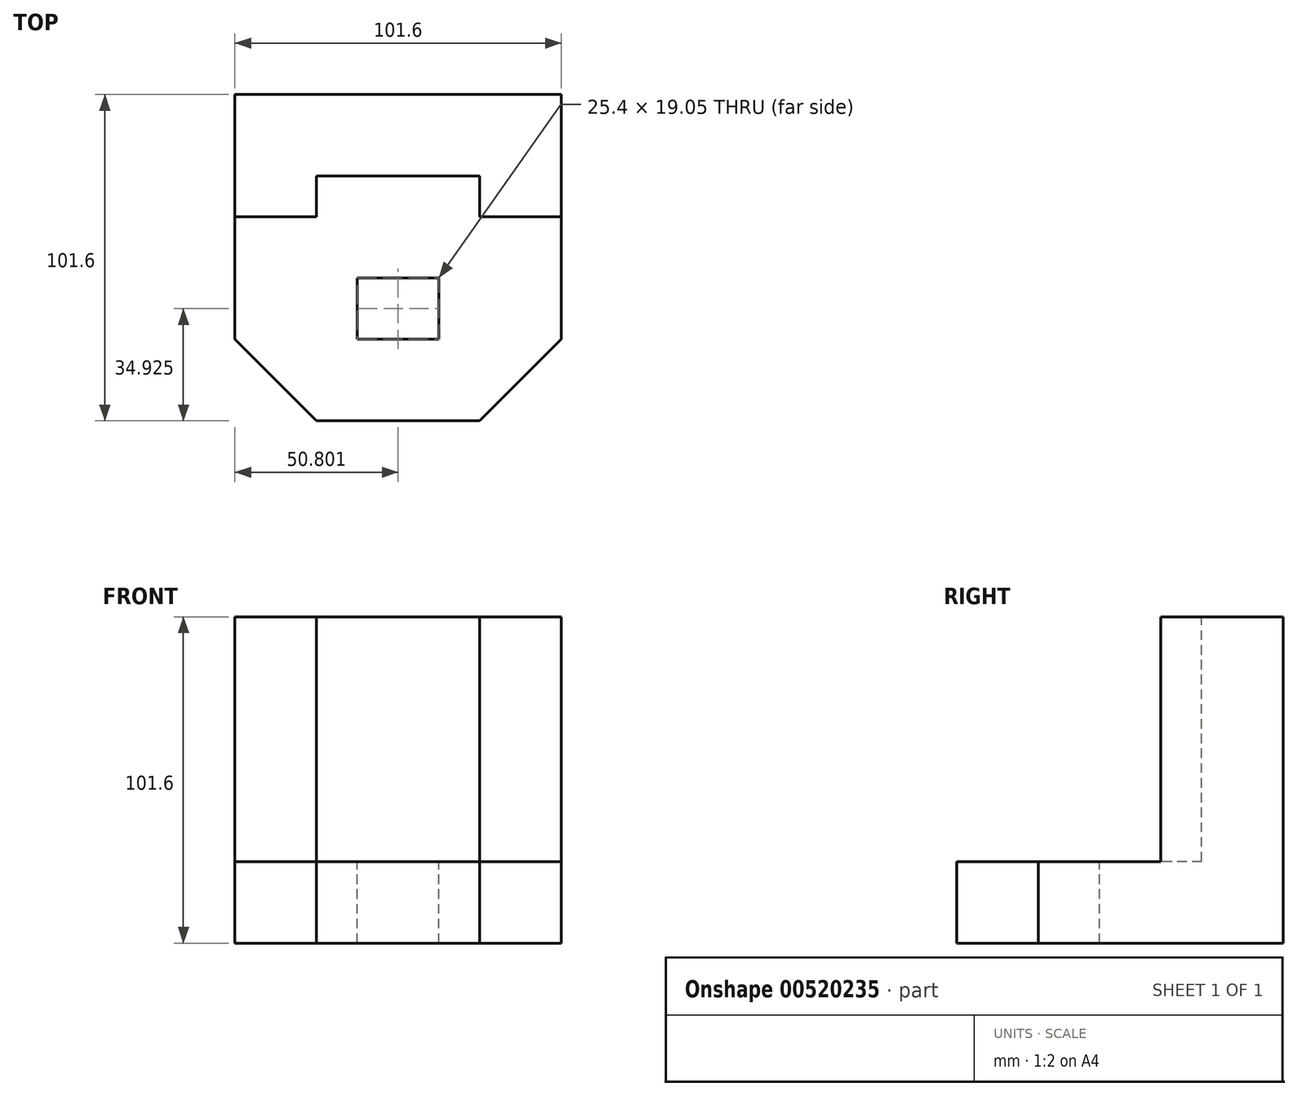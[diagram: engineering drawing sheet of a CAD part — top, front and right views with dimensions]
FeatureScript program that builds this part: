
annotation { "Feature Type Name" : "Feature", "Feature Type Description" : "" }
export const myFeature = defineFeature(function(context is Context, id is Id, definition is map)
    precondition{}
    {
        {
            var Q0;
            Q0=qCreatedBy(makeId("Front.planeOp"),FACE);
            var sketch = newSketch(context, id + "F0", { "sketchPlane" : qUnion([Q0])});
            skLineSegment(sketch, "E0.bottom", {"start": v(-47, -44.76) * mm, "end": v(54.6, -44.76) * mm});
            skLineSegment(sketch, "E0.top", {"start": v(-47, 56.84) * mm, "end": v(54.6, 56.84) * mm});
            skLineSegment(sketch, "E0.left", {"start": v(-47, -44.76) * mm, "end": v(-47, 56.84) * mm});
            skLineSegment(sketch, "E0.right", {"start": v(54.6, -44.76) * mm, "end": v(54.6, 56.84) * mm});
            skSolve(sketch);
        }
        {
            var Q0;
            Q0=makeQuery(id+"F0.imprint","IMPRINT",FACE,{"disambiguationData":[TD([[makeQuery(id+"F0.imprint","IMPRINT",EDGE,{"derivedFrom":sQuery(id+"F0.wireOp",EDGE,"E0.bottom")}),1.0]])]});
            extrude(context, id + "F1", {"entities" : qUnion([Q0]), "depth" : 101.6 * mm, "offsetDistance" : 25.4 * mm});
        }
        {
            var Q0;
            Q0=makeQuery(id+"F1.opExtrude","CAP_FACE",FACE,{"disambiguationData":[OSD([sQuery(id+"F0.wireOp",EDGE,"E0.bottom"),sQuery(id+"F0.wireOp",EDGE,"E0.top"),sQuery(id+"F0.wireOp",EDGE,"E0.left"),sQuery(id+"F0.wireOp",EDGE,"E0.right")])],"isStart":false});
            var sketch = newSketch(context, id + "F2", { "sketchPlane" : qUnion([Q0])});
            skLineSegment(sketch, "E1.bottom", {"start": v(-47, -19.36) * mm, "end": v(-21.6, -19.36) * mm});
            skLineSegment(sketch, "E1.top", {"start": v(-47, 56.84) * mm, "end": v(-21.6, 56.84) * mm});
            skLineSegment(sketch, "E1.left", {"start": v(-47, -19.36) * mm, "end": v(-47, 56.84) * mm});
            skLineSegment(sketch, "E1.right", {"start": v(-21.6, -19.36) * mm, "end": v(-21.6, 56.84) * mm});
            skLineSegment(sketch, "E2.bottom", {"start": v(54.6, -19.36) * mm, "end": v(29.2, -19.36) * mm});
            skLineSegment(sketch, "E2.top", {"start": v(54.6, 56.84) * mm, "end": v(29.2, 56.84) * mm});
            skLineSegment(sketch, "E2.left", {"start": v(54.6, -19.36) * mm, "end": v(54.6, 56.84) * mm});
            skLineSegment(sketch, "E2.right", {"start": v(29.2, -19.36) * mm, "end": v(29.2, 56.84) * mm});
            skLineSegment(sketch, "E3.bottom", {"start": v(-21.6, 56.84) * mm, "end": v(29.2, 56.84) * mm});
            skLineSegment(sketch, "E3.top", {"start": v(-21.6, -19.36) * mm, "end": v(29.2, -19.36) * mm});
            skLineSegment(sketch, "E3.left", {"start": v(-21.6, 56.84) * mm, "end": v(-21.6, -19.36) * mm});
            skLineSegment(sketch, "E3.right", {"start": v(29.2, 56.84) * mm, "end": v(29.2, -19.36) * mm});
            skSolve(sketch);
        }
        {
            var Q0;
            Q0=makeQuery(id+"F2.imprint","IMPRINT",FACE,{"disambiguationData":[TD([[makeQuery(id+"F2.imprint","IMPRINT",EDGE,{"derivedFrom":sQuery(id+"F2.wireOp",EDGE,"E3.bottom")}),-1.0]])]});
            extrude(context, id + "F3", {"entities" : qUnion([Q0]), "operationType" : NewBodyOperationType.REMOVE, "oppositeDirection" : true, "depth" : 76.2 * mm, "offsetDistance" : 25.4 * mm});
        }
        {
            var Q0;
            Q0=makeQuery(id+"F1.opExtrude","CAP_FACE",FACE,{"disambiguationData":[OSD([sQuery(id+"F0.wireOp",EDGE,"E0.bottom"),sQuery(id+"F0.wireOp",EDGE,"E0.top"),sQuery(id+"F0.wireOp",EDGE,"E0.left"),sQuery(id+"F0.wireOp",EDGE,"E0.right")])],"isStart":false});
            var sketch = newSketch(context, id + "F4", { "sketchPlane" : qUnion([Q0])});
            skLineSegment(sketch, "E4.bottom", {"start": v(-21.6, -19.36) * mm, "end": v(-47, -19.36) * mm});
            skLineSegment(sketch, "E4.top", {"start": v(-21.6, 56.84) * mm, "end": v(-47, 56.84) * mm});
            skLineSegment(sketch, "E4.left", {"start": v(-21.6, -19.36) * mm, "end": v(-21.6, 56.84) * mm});
            skLineSegment(sketch, "E4.right", {"start": v(-47, -19.36) * mm, "end": v(-47, 56.84) * mm});
            skLineSegment(sketch, "E5.bottom", {"start": v(29.2, -19.36) * mm, "end": v(54.6, -19.36) * mm});
            skLineSegment(sketch, "E5.top", {"start": v(29.2, 56.84) * mm, "end": v(54.6, 56.84) * mm});
            skLineSegment(sketch, "E5.left", {"start": v(29.2, -19.36) * mm, "end": v(29.2, 56.84) * mm});
            skLineSegment(sketch, "E5.right", {"start": v(54.6, -19.36) * mm, "end": v(54.6, 56.84) * mm});
            skSolve(sketch);
        }
        {
            var Q0;
            Q0=makeQuery(id+"F4.imprint","IMPRINT",FACE,{"disambiguationData":[TD([[makeQuery(id+"F4.imprint","IMPRINT",EDGE,{"derivedFrom":sQuery(id+"F4.wireOp",EDGE,"E5.bottom")}),1.0]])]});
            var Q1;
            Q1=makeQuery(id+"F4.imprint","IMPRINT",FACE,{"disambiguationData":[TD([[makeQuery(id+"F4.imprint","IMPRINT",EDGE,{"derivedFrom":sQuery(id+"F4.wireOp",EDGE,"E4.bottom")}),-1.0]])]});
            extrude(context, id + "F5", {"entities" : qUnion([Q0, Q1]), "operationType" : NewBodyOperationType.REMOVE, "oppositeDirection" : true, "depth" : 63.5 * mm, "offsetDistance" : 25.4 * mm});
        }
        {
            var Q0;
            Q0=makeQuery(id+"F5.boolean.opBoolean","MERGE",FACE,{"derivedFrom":[makeQuery(id+"F3.boolean.opBoolean","COPY",FACE,{"derivedFrom":makeQuery(id+"F3.opExtrude","SWEPT_FACE",FACE,{"disambiguationData":[OSD([sQuery(id+"F2.wireOp",EDGE,"E3.top")])]})}),makeQuery(id+"F5.opExtrude","SWEPT_FACE",FACE,{"disambiguationData":[OSD([sQuery(id+"F4.wireOp",EDGE,"E4.bottom")])]}),makeQuery(id+"F5.opExtrude","SWEPT_FACE",FACE,{"disambiguationData":[OSD([sQuery(id+"F4.wireOp",EDGE,"E5.bottom")])]})]});
            var sketch = newSketch(context, id + "F6", { "sketchPlane" : qUnion([Q0])});
            skLineSegment(sketch, "E6", {"start": v(54.6, -101.6) * mm, "end": v(54.6, -76.2) * mm});
            skLineSegment(sketch, "E7", {"start": v(54.6, -101.6) * mm, "end": v(29.2, -101.6) * mm});
            skLineSegment(sketch, "E8", {"start": v(29.2, -101.6) * mm, "end": v(54.6, -76.2) * mm});
            skSolve(sketch);
        }
        {
            var Q0;
            Q0 = qSketchRegion(id + "F6", true);
            extrude(context, id + "F7", {"entities" : qUnion([Q0]), "operationType" : NewBodyOperationType.REMOVE, "oppositeDirection" : true, "depth" : 25.4 * mm, "offsetDistance" : 25.4 * mm});
        }
        {
            var Q0;
            Q0=makeQuery(id+"F5.boolean.opBoolean","MERGE",FACE,{"derivedFrom":[makeQuery(id+"F3.boolean.opBoolean","COPY",FACE,{"derivedFrom":makeQuery(id+"F3.opExtrude","SWEPT_FACE",FACE,{"disambiguationData":[OSD([sQuery(id+"F2.wireOp",EDGE,"E3.top")])]})}),makeQuery(id+"F5.opExtrude","SWEPT_FACE",FACE,{"disambiguationData":[OSD([sQuery(id+"F4.wireOp",EDGE,"E4.bottom")])]}),makeQuery(id+"F5.opExtrude","SWEPT_FACE",FACE,{"disambiguationData":[OSD([sQuery(id+"F4.wireOp",EDGE,"E5.bottom")])]})]});
            var sketch = newSketch(context, id + "F8", { "sketchPlane" : qUnion([Q0])});
            skLineSegment(sketch, "E9", {"start": v(-47, -101.6) * mm, "end": v(-21.6, -101.6) * mm});
            skLineSegment(sketch, "E10", {"start": v(-47, -101.6) * mm, "end": v(-47, -76.2) * mm});
            skLineSegment(sketch, "E11", {"start": v(-47, -76.2) * mm, "end": v(-21.6, -101.6) * mm});
            skSolve(sketch);
        }
        {
            var Q0;
            Q0=makeQuery(id+"F8.imprint","IMPRINT",FACE,{"disambiguationData":[TD([[makeQuery(id+"F8.imprint","IMPRINT",EDGE,{"derivedFrom":sQuery(id+"F8.wireOp",EDGE,"E9")}),1.0]])]});
            extrude(context, id + "F9", {"entities" : qUnion([Q0]), "operationType" : NewBodyOperationType.REMOVE, "oppositeDirection" : true, "depth" : 25.4 * mm, "offsetDistance" : 25.4 * mm});
        }
        {
            var Q0;
            Q0=makeQuery(id+"F5.boolean.opBoolean","MERGE",FACE,{"derivedFrom":[makeQuery(id+"F3.boolean.opBoolean","COPY",FACE,{"derivedFrom":makeQuery(id+"F3.opExtrude","SWEPT_FACE",FACE,{"disambiguationData":[OSD([sQuery(id+"F2.wireOp",EDGE,"E3.top")])]})}),makeQuery(id+"F5.opExtrude","SWEPT_FACE",FACE,{"disambiguationData":[OSD([sQuery(id+"F4.wireOp",EDGE,"E4.bottom")])]}),makeQuery(id+"F5.opExtrude","SWEPT_FACE",FACE,{"disambiguationData":[OSD([sQuery(id+"F4.wireOp",EDGE,"E5.bottom")])]})]});
            var sketch = newSketch(context, id + "F10", { "sketchPlane" : qUnion([Q0])});
            skLineSegment(sketch, "E12", {"start": v(-8.9, -57.15) * mm, "end": v(16.5, -57.15) * mm});
            skPoint(sketch, "E12.endSnap0", {"position": v(54.6, -57.15) * mm});
            skLineSegment(sketch, "E13", {"start": v(-8.9, -57.15) * mm, "end": v(-8.9, -76.2) * mm});
            skLineSegment(sketch, "E14", {"start": v(-8.9, -76.2) * mm, "end": v(16.5, -76.2) * mm});
            skLineSegment(sketch, "E15", {"start": v(16.5, -76.2) * mm, "end": v(16.5, -57.15) * mm});
            skSolve(sketch);
        }
        {
            var Q0;
            Q0=makeQuery(id+"F10.imprint","IMPRINT",FACE,{"disambiguationData":[TD([[makeQuery(id+"F10.imprint","IMPRINT",EDGE,{"derivedFrom":sQuery(id+"F10.wireOp",EDGE,"E12")}),-1.0]])]});
            extrude(context, id + "F11", {"entities" : qUnion([Q0]), "operationType" : NewBodyOperationType.REMOVE, "oppositeDirection" : true, "depth" : 25.4 * mm, "offsetDistance" : 25.4 * mm});
        }
    });
